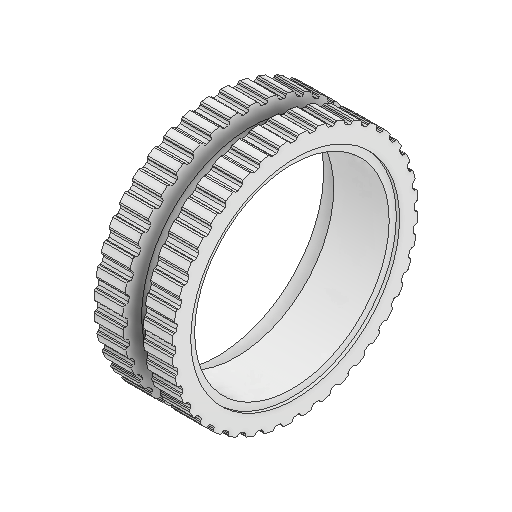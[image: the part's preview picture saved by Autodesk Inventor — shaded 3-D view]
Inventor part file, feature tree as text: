
AUTODESK INVENTOR PART (.ipt)
format: ipt  version: 2025 (Build 290162000, 162)  size: 1,557,504 bytes
history: native  units: in
note: dims shown in document units (in); Inventor stores cm internally (conversion verified against a paired STEP export)
features: sketch x4, other x4, extrude x3, reference x2, revolve x1, mirror x1
ambient origin geometry x8: Origin, YZ Plane, XZ Plane, XY Plane, X Axis, Y Axis, Z Axis, Center Point
bodies: Solid1 (feature_tree)
feature tree (15):
  extrude  "Extrusion1"  Depth=2.0in TaperAngle=0.0deg
  revolve  "Revolution1"  [1 undecoded]
  mirror  "Mirror1"
  extrude  "Extrusion2"  TaperAngle=90.0deg  [1 undecoded]
  extrude  "Extrusion3"  Depth=0.5in TaperAngle=0.0deg
  sketch  "Sketch1"  dims[d0=4.97in d1=2.0in d2=0.0in]
  reference  "Reference1"
  reference  "Reference2"
  sketch  "Sketch2"  dims[d3=0.131in d4=0.262in]
  sketch  "Sketch3"  dims[d5=0.35in d6=90.0deg]
  sketch  "Sketch4"  dims[d7=5.4528in d8=0.5in d9=0.0in d10=5.3346in d11=0.0827in d12=0.0in]
  other  "<userpath>\Desktop\puppycat\v1.iam"
  other  "v1.iam"
  other  "6495K821_Timing Belt Pulley:1"
  other  "6495K822_Timing Belt Pulley:1"
note: 2 required parameter values undecoded (feature->parameter linkage not recoverable at this tier; creation-order binding heuristic only, values carry confidence <= 0.55)